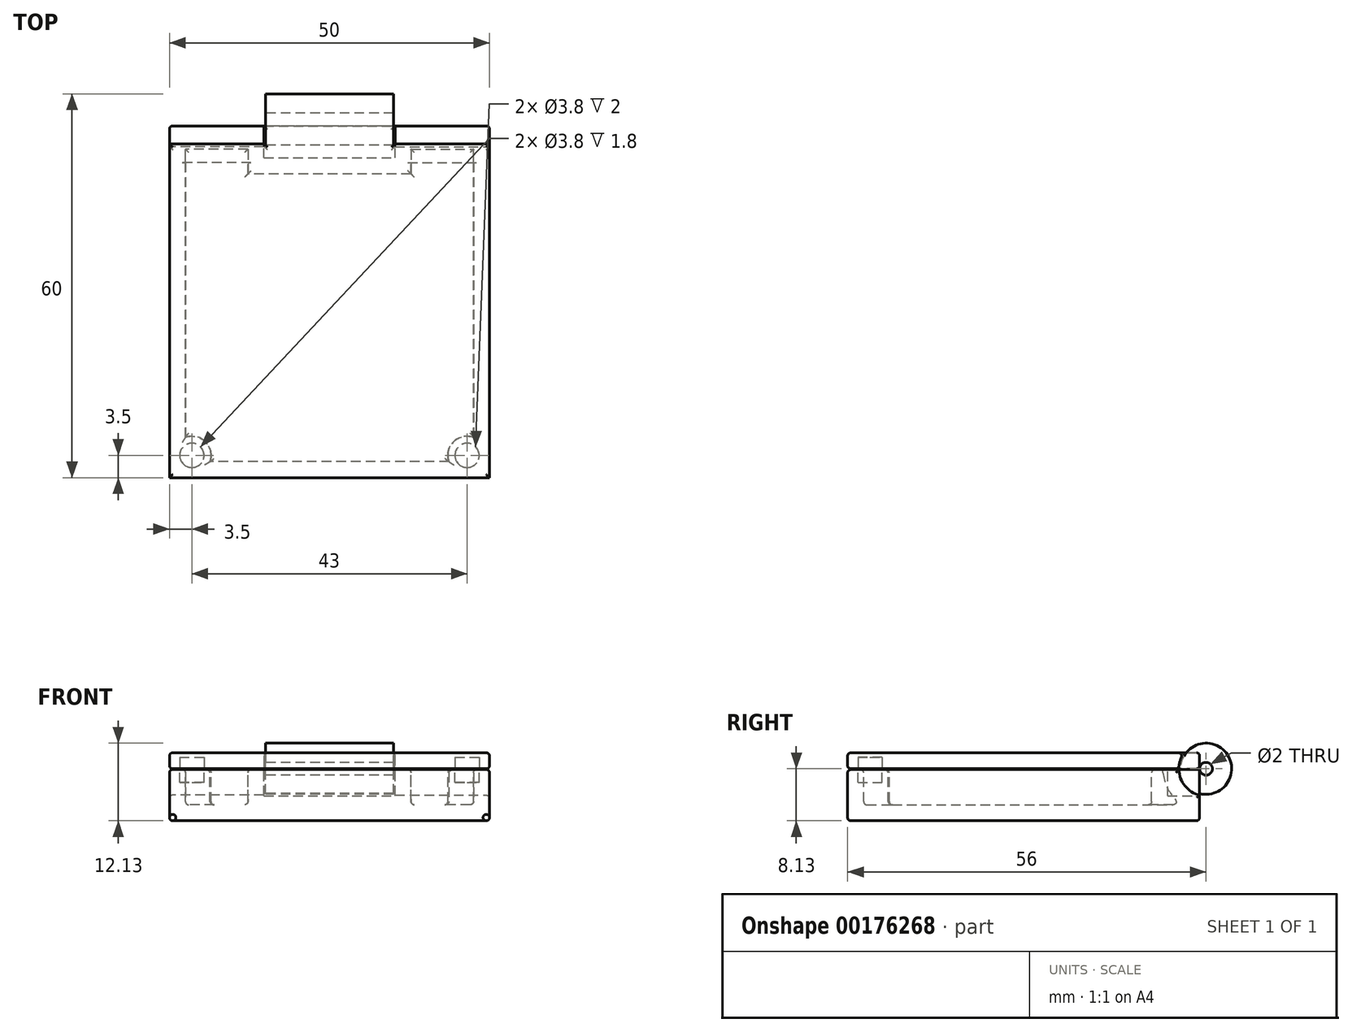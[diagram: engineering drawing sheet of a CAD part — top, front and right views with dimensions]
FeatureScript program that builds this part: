
annotation { "Feature Type Name" : "Feature", "Feature Type Description" : "" }
export const myFeature = defineFeature(function(context is Context, id is Id, definition is map)
    precondition{}
    {
        {
            var Q0;
            Q0=qCreatedBy(makeId("Right.planeOp"),FACE);
            var sketch = newSketch(context, id + "F0", { "sketchPlane" : qUnion([Q0])});
            skCircle(sketch, "E0", {"center": v(0, 0) * mm, "radius": 1 * mm});
            skCircle(sketch, "E1.0", {"center": v(0, 0) * mm, "radius": 4 * mm});
            skSolve(sketch);
        }
        {
            var Q0;
            Q0=qCreatedBy(makeId("Right.planeOp"),FACE);
            var sketch = newSketch(context, id + "F1", { "sketchPlane" : qUnion([Q0])});
            skCircle(sketch, "E2.0", {"center": v(0, 0) * mm, "radius": 1 * mm, "construction": true});
            skLineSegment(sketch, "E3", {"start": v(-1, -0.12) * mm, "end": v(-56, -0.13) * mm});
            skLineSegment(sketch, "E4", {"start": v(-56, -0.13) * mm, "end": v(-56, -8.13) * mm});
            skLineSegment(sketch, "E5", {"start": v(-56, -8.13) * mm, "end": v(-1, -8.12) * mm});
            skLineSegment(sketch, "E6", {"start": v(-1, -8.12) * mm, "end": v(-1, -0.12) * mm});
            skLineSegment(sketch, "E7", {"start": v(0, 0) * mm, "end": v(-37.05, 0) * mm, "construction": true});
            skSolve(sketch);
        }
        {
            var Q0;
            Q0=qCreatedBy(makeId("Right.planeOp"),FACE);
            var sketch = newSketch(context, id + "F2", { "sketchPlane" : qUnion([Q0])});
            skArc(sketch, "E8.0", {"start": v(-1, 0) * mm, "mid": v(-1, -0.06) * mm, "end": v(-1, -0.12) * mm});
            skLineSegment(sketch, "E9", {"start": v(-1, 0) * mm, "end": v(-56, 0) * mm});
            skLineSegment(sketch, "E10", {"start": v(-56, 0) * mm, "end": v(-56, 2.5) * mm});
            skLineSegment(sketch, "E11", {"start": v(-56, 2.5) * mm, "end": v(-1, 2.5) * mm});
            skLineSegment(sketch, "E12", {"start": v(-1, 2.5) * mm, "end": v(-1, 0) * mm});
            skPoint(sketch, "E13.0.end.orphan", {"position": v(-1, -0.12) * mm});
            skPoint(sketch, "E13.0.start.orphan", {"position": v(-1, -8.12) * mm});
            skSolve(sketch);
        }
        {
            var Q0;
            Q0 = qSketchRegion(id + "F0", true);
            extrude(context, id + "F3", {"entities" : qUnion([Q0]), "depth" : 10 * mm, "hasSecondDirection" : true, "secondDirectionOppositeDirection" : true, "secondDirectionDepth" : 10 * mm});
        }
        {
            var Q0;
            Q0 = qSketchRegion(id + "F2", true);
            var Q1;
            Q1 = qSketchRegion(id + "F1", true);
            extrude(context, id + "F4", {"entities" : qUnion([Q0, Q1]), "depth" : 25 * mm, "hasSecondDirection" : true, "secondDirectionOppositeDirection" : true, "secondDirectionDepth" : 25 * mm});
        }
        {
            var Q0;
            Q0=makeQuery(id+"F4.opExtrude","SWEPT_FACE",FACE,{"disambiguationData":[OSD([sQuery(id+"F1.wireOp",EDGE,"E6")])]});
            var sketch = newSketch(context, id + "F5", { "sketchPlane" : qUnion([Q0])});
            skLineSegment(sketch, "E14.0", {"start": v(-10.25, -4.25) * mm, "end": v(-10.25, -0.12) * mm});
            skLineSegment(sketch, "E14.1", {"start": v(10.25, -4.25) * mm, "end": v(-10.25, -4.25) * mm});
            skLineSegment(sketch, "E14.2", {"start": v(10.25, -4.25) * mm, "end": v(10.25, -0.12) * mm});
            skPoint(sketch, "E15.0.end.orphan", {"position": v(-10, 4) * mm});
            skPoint(sketch, "E15.0.start.orphan", {"position": v(-10, -4) * mm});
            skPoint(sketch, "E16.0.end.orphan", {"position": v(10, 4) * mm});
            skPoint(sketch, "E16.0.start.orphan", {"position": v(10, -4) * mm});
            skLineSegment(sketch, "E17.0", {"start": v(-10.25, -0.12) * mm, "end": v(10.25, -0.12) * mm});
            skPoint(sketch, "E18.orphan", {"position": v(-25, -0.12) * mm});
            skPoint(sketch, "E19.orphan", {"position": v(25, -0.12) * mm});
            skSolve(sketch);
        }
        {
            var Q0;
            Q0 = qSketchRegion(id + "F5", true);
            extrude(context, id + "F6", {"entities" : qUnion([Q0]), "operationType" : NewBodyOperationType.REMOVE, "oppositeDirection" : true, "depth" : 5 * mm});
        }
        {
            var Q0;
            Q0=makeQuery(id+"F3.opExtrude","CAP_FACE",FACE,{"disambiguationData":[OSD([sQuery(id+"F0.wireOp",EDGE,"E0"),sQuery(id+"F0.wireOp",EDGE,"E1.0")])],"isStart":false});
            cPlane(context, id + "F7", {"entities" : qUnion([Q0]), "cplaneType" : CPlaneType.OFFSET, "offset" : .5 * mm, "width" : 150 * mm, "height" : 150 * mm});
        }
        {
            var Q0;
            Q0=qCreatedBy(id+"F7.planeOp",FACE);
            var sketch = newSketch(context, id + "F8", { "sketchPlane" : qUnion([Q0])});
            skCircle(sketch, "E20.0", {"center": v(0, 0) * mm, "radius": 4 * mm});
            skCircle(sketch, "E21.0", {"center": v(0, 0) * mm, "radius": 1 * mm});
            skSolve(sketch);
        }
        {
            var Q0;
            Q0 = qSketchRegion(id + "F8", true);
            var Q1;
            Q1=makeQuery(id+"F4.opExtrude","CAP_FACE",FACE,{"disambiguationData":[OSD([sQuery(id+"F1.wireOp",EDGE,"E3"),sQuery(id+"F1.wireOp",EDGE,"E4"),sQuery(id+"F1.wireOp",EDGE,"E5"),sQuery(id+"F1.wireOp",EDGE,"E6")])],"isStart":false});
            extrude(context, id + "F9", {"entities" : qUnion([Q0]), "endBound" : BoundingType.UP_TO_SURFACE, "endBoundEntityFace" : qUnion([Q1]), "depth" : 25 * mm});
        }
        {
            var Q0;
            Q0=makeQuery(id+"F9.opExtrude","SWEPT_BODY",BODY,{"disambiguationData":[OSD([sQuery(id+"F8.wireOp",EDGE,"E20.0"),sQuery(id+"F8.wireOp",EDGE,"E21.0")])]});
            var Q1;
            Q1=qCreatedBy(makeId("Right.planeOp"),FACE);
            mirror(context, id + "F10", {"entities" : qUnion([Q0]), "mirrorPlane" : qUnion([Q1])});
        }
        {
            var Q0;
            Q0=makeQuery(id+"F4.opExtrude","CAP_FACE",FACE,{"disambiguationData":[OSD([sQuery(id+"F2.wireOp",EDGE,"E9"),sQuery(id+"F2.wireOp",EDGE,"E10"),sQuery(id+"F2.wireOp",EDGE,"E11"),sQuery(id+"F2.wireOp",EDGE,"E12")])],"isStart":false});
            var sketch = newSketch(context, id + "F11", { "sketchPlane" : qUnion([Q0])});
            skCircle(sketch, "E22.0", {"center": v(0, 0) * mm, "radius": 4.25 * mm});
            skSolve(sketch);
        }
        {
            var Q0;
            Q0 = qSketchRegion(id + "F11", true);
            extrude(context, id + "F12", {"entities" : qUnion([Q0]), "operationType" : NewBodyOperationType.REMOVE, "oppositeDirection" : true, "depth" : 14.8 * mm});
        }
        {
            var Q0;
            Q0=makeQuery(id+"F4.opExtrude","CAP_FACE",FACE,{"disambiguationData":[OSD([sQuery(id+"F1.wireOp",EDGE,"E3"),sQuery(id+"F1.wireOp",EDGE,"E4"),sQuery(id+"F1.wireOp",EDGE,"E5"),sQuery(id+"F1.wireOp",EDGE,"E6")])],"isStart":true});
            var sketch = newSketch(context, id + "F13", { "sketchPlane" : qUnion([Q0])});
            skCircle(sketch, "E23.0", {"center": v(0, 0) * mm, "radius": 4.25 * mm});
            skSolve(sketch);
        }
        {
            var Q0;
            Q0 = qSketchRegion(id + "F13", true);
            extrude(context, id + "F14", {"entities" : qUnion([Q0]), "operationType" : NewBodyOperationType.REMOVE, "oppositeDirection" : true, "depth" : 14.8 * mm});
        }
        {
            var Q0;
            Q0=makeQuery(id+"F4.opExtrude","SWEPT_FACE",FACE,{"disambiguationData":[OSD([sQuery(id+"F1.wireOp",EDGE,"E3")])]});
            shell(context, id + "F15", {"entities" : qUnion([Q0]), "thickness" : 2.5 * mm});
        }
        {
            var Q0;
            Q0=makeQuery(id+"F4.opExtrude","SWEPT_FACE",FACE,{"disambiguationData":[OSD([sQuery(id+"F1.wireOp",EDGE,"E3")])]});
            cPlane(context, id + "F16", {"entities" : qUnion([Q0]), "cplaneType" : CPlaneType.OFFSET, "offset" : 0 * mm, "width" : 150 * mm, "height" : 150 * mm});
        }
        {
            var Q0;
            Q0=qCreatedBy(id+"F16.planeOp",FACE);
            var sketch = newSketch(context, id + "F17", { "sketchPlane" : qUnion([Q0])});
            skPoint(sketch, "E24.0", {"position": v(-22.5, -53.5) * mm});
            skPoint(sketch, "E25", {"position": v(-21.5, -52.5) * mm});
            skCircle(sketch, "E26", {"center": v(-21.5, -52.5) * mm, "radius": 3 * mm, "construction": true});
            skCircle(sketch, "E27", {"center": v(-21.5, -52.5) * mm, "radius": 1.9 * mm, "construction": true});
            skLineSegment(sketch, "E28", {"start": v(0, 0) * mm, "end": v(0, -89.25) * mm, "construction": true});
            skCircle(sketch, "E29.MirrorC", {"center": v(21.5, -52.5) * mm, "radius": 3 * mm, "construction": true});
            skCircle(sketch, "E30.MirrorC", {"center": v(21.5, -52.5) * mm, "radius": 1.9 * mm, "construction": true});
            skSolve(sketch);
        }
        {
            var Q0;
            Q0=qCreatedBy(id+"F16.planeOp",FACE);
            var sketch = newSketch(context, id + "F18", { "sketchPlane" : qUnion([Q0])});
            skCircle(sketch, "E31.0", {"center": v(-21.5, -52.5) * mm, "radius": 3 * mm});
            skCircle(sketch, "E32.0", {"center": v(21.5, -52.5) * mm, "radius": 3 * mm});
            skSolve(sketch);
        }
        {
            var Q0;
            Q0 = qSketchRegion(id + "F18", true);
            extrude(context, id + "F19", {"entities" : qUnion([Q0]), "operationType" : NewBodyOperationType.ADD, "endBound" : BoundingType.UP_TO_NEXT, "oppositeDirection" : true, "depth" : 25 * mm});
        }
        {
            var Q0;
            Q0=qCreatedBy(id+"F16.planeOp",FACE);
            var sketch = newSketch(context, id + "F20", { "sketchPlane" : qUnion([Q0])});
            skCircle(sketch, "E33.0", {"center": v(-21.5, -52.5) * mm, "radius": 1.9 * mm});
            skCircle(sketch, "E34.0", {"center": v(21.5, -52.5) * mm, "radius": 1.9 * mm});
            skSolve(sketch);
        }
        {
            var Q0;
            Q0 = qSketchRegion(id + "F20", true);
            extrude(context, id + "F21", {"entities" : qUnion([Q0]), "operationType" : NewBodyOperationType.REMOVE, "oppositeDirection" : true, "depth" : 2 * mm});
        }
        {
            var Q0;
            Q0=makeQuery(id+"F15.opShell","OFFSET_FACE",FACE,{"disambiguationData":[OSD([sQuery(id+"F1.wireOp",EDGE,"E5")])]});
            var Q1;
            Q1=makeQuery(id+"F4.opExtrude","SWEPT_FACE",FACE,{"disambiguationData":[OSD([sQuery(id+"F1.wireOp",EDGE,"E4")])]});
            var Q2;
            Q2=makeQuery(id+"F4.opExtrude","CAP_FACE",FACE,{"disambiguationData":[OSD([sQuery(id+"F1.wireOp",EDGE,"E3"),sQuery(id+"F1.wireOp",EDGE,"E4"),sQuery(id+"F1.wireOp",EDGE,"E5"),sQuery(id+"F1.wireOp",EDGE,"E6")])],"isStart":false});
            var Q3;
            Q3=makeQuery(id+"F4.opExtrude","CAP_FACE",FACE,{"disambiguationData":[OSD([sQuery(id+"F1.wireOp",EDGE,"E3"),sQuery(id+"F1.wireOp",EDGE,"E4"),sQuery(id+"F1.wireOp",EDGE,"E5"),sQuery(id+"F1.wireOp",EDGE,"E6")])],"isStart":true});
            var Q4;
            Q4=makeQuery(id+"F4.opExtrude","SWEPT_EDGE",EDGE,{"disambiguationData":[OSD([sQuery(id+"F1.wireOp",EDGE,"E5"),sQuery(id+"F1.wireOp",EDGE,"E6")])]});
            var Q5;
            Q5=makeQuery(id+"F9.opExtrude","CAP_EDGE",EDGE,{"disambiguationData":[OSD([sQuery(id+"F8.wireOp",EDGE,"E20.0")])],"isStart":false});
            var Q6;
            Q6=makeQuery(id+"F10.opPattern","COPY",EDGE,{"derivedFrom":makeQuery(id+"F9.opExtrude","CAP_EDGE",EDGE,{"disambiguationData":[OSD([sQuery(id+"F8.wireOp",EDGE,"E20.0")])],"isStart":false}),"instanceName":"1"});
            var Q7;
            {var subQ0=sQuery(id+"F1.wireOp",EDGE,"E3");Q7=makeQuery(id+"F15.opShell","OFFSET_EDGE",EDGE,{"disambiguationData":[OSD([subQ0]),TDD([makeQuery(id+"F4.opExtrude","CAP_EDGE",EDGE,{"disambiguationData":[OSD([subQ0])],"isStart":true})])]});}
            var Q8;
            Q8=makeQuery(id+"F19.opExtrude","CAP_EDGE",EDGE,{"disambiguationData":[OSD([sQuery(id+"F18.wireOp",EDGE,"E31.0")])],"isStart":true});
            var Q9;
            Q9=makeQuery(id+"F15.opShell","OFFSET_EDGE",EDGE,{"disambiguationData":[OSD([sQuery(id+"F1.wireOp",EDGE,"E3"),sQuery(id+"F1.wireOp",EDGE,"E4")])]});
            var Q10;
            Q10=makeQuery(id+"F19.opExtrude","CAP_EDGE",EDGE,{"disambiguationData":[OSD([sQuery(id+"F18.wireOp",EDGE,"E32.0")])],"isStart":true});
            var Q11;
            {var subQ0=sQuery(id+"F1.wireOp",EDGE,"E3");Q11=makeQuery(id+"F15.opShell","OFFSET_EDGE",EDGE,{"disambiguationData":[OSD([subQ0]),TDD([makeQuery(id+"F4.opExtrude","CAP_EDGE",EDGE,{"disambiguationData":[OSD([subQ0])],"isStart":false})])]});}
            var Q12;
            Q12=makeQuery(id+"F15.opShell","OFFSET_EDGE",EDGE,{"disambiguationData":[OSD([sQuery(id+"F1.wireOp",EDGE,"E3"),sQuery(id+"F1.wireOp",EDGE,"E6"),sQuery(id+"F5.wireOp",EDGE,"E14.2"),sQuery(id+"F5.wireOp",EDGE,"E17.0")])]});
            var Q13;
            Q13=makeQuery(id+"F15.opShell","OFFSET_EDGE",EDGE,{"disambiguationData":[OSD([sQuery(id+"F5.wireOp",EDGE,"E17.0")])]});
            var Q14;
            Q14=makeQuery(id+"F15.opShell","OFFSET_EDGE",EDGE,{"disambiguationData":[OSD([sQuery(id+"F1.wireOp",EDGE,"E3"),sQuery(id+"F1.wireOp",EDGE,"E6"),sQuery(id+"F5.wireOp",EDGE,"E14.0"),sQuery(id+"F5.wireOp",EDGE,"E17.0")])]});
            var Q15;
            Q15=makeQuery(id+"F6.boolean.opBoolean","COPY",EDGE,{"derivedFrom":makeQuery(id+"F6.opExtrude","CAP_EDGE",EDGE,{"disambiguationData":[OSD([sQuery(id+"F5.wireOp",EDGE,"E17.0")])],"isStart":false})});
            var Q16;
            Q16=makeQuery(id+"F6.boolean.opBoolean","COPY",EDGE,{"derivedFrom":makeQuery(id+"F6.opExtrude","SWEPT_EDGE",EDGE,{"disambiguationData":[OSD([sQuery(id+"F1.wireOp",EDGE,"E3"),sQuery(id+"F1.wireOp",EDGE,"E6"),sQuery(id+"F5.wireOp",EDGE,"E14.0"),sQuery(id+"F5.wireOp",EDGE,"E17.0")])]})});
            var Q17;
            Q17=makeQuery(id+"F6.boolean.opBoolean","COPY",EDGE,{"derivedFrom":makeQuery(id+"F6.opExtrude","SWEPT_EDGE",EDGE,{"disambiguationData":[OSD([sQuery(id+"F1.wireOp",EDGE,"E3"),sQuery(id+"F1.wireOp",EDGE,"E6"),sQuery(id+"F5.wireOp",EDGE,"E14.2"),sQuery(id+"F5.wireOp",EDGE,"E17.0")])]})});
            fillet(context, id + "F22", {"entities" : qUnion([Q0, Q1, Q2, Q3, Q4, Q5, Q6, Q7, Q8, Q9, Q10, Q11, Q12, Q13, Q14, Q15, Q16, Q17]), "radius" : .5 * mm, "tangentPropagation" : true, "allowEdgeOverflow" : false});
        }
        {
            var Q0;
            Q0=makeQuery(id+"F4.opExtrude","SWEPT_FACE",FACE,{"disambiguationData":[OSD([sQuery(id+"F2.wireOp",EDGE,"E11")])]});
            var Q1;
            Q1=makeQuery(id+"F4.opExtrude","SWEPT_FACE",FACE,{"disambiguationData":[OSD([sQuery(id+"F2.wireOp",EDGE,"E9")])]});
            fillet(context, id + "F23", {"entities" : qUnion([Q0, Q1]), "radius" : .5 * mm, "tangentPropagation" : true, "allowEdgeOverflow" : false});
        }
        {
            var Q0;
            Q0=makeQuery(id+"F4.opExtrude","SWEPT_FACE",FACE,{"disambiguationData":[OSD([sQuery(id+"F2.wireOp",EDGE,"E9")])]});
            var sketch = newSketch(context, id + "F24", { "sketchPlane" : qUnion([Q0])});
            skCircle(sketch, "E35.0", {"center": v(21.5, 52.5) * mm, "radius": 1.9 * mm});
            skCircle(sketch, "E36.0", {"center": v(-21.5, 52.5) * mm, "radius": 1.9 * mm});
            skSolve(sketch);
        }
        {
            var Q0;
            Q0 = qSketchRegion(id + "F24", true);
            extrude(context, id + "F25", {"entities" : qUnion([Q0]), "operationType" : NewBodyOperationType.REMOVE, "oppositeDirection" : true, "depth" : 1.8 * mm});
        }
    });
